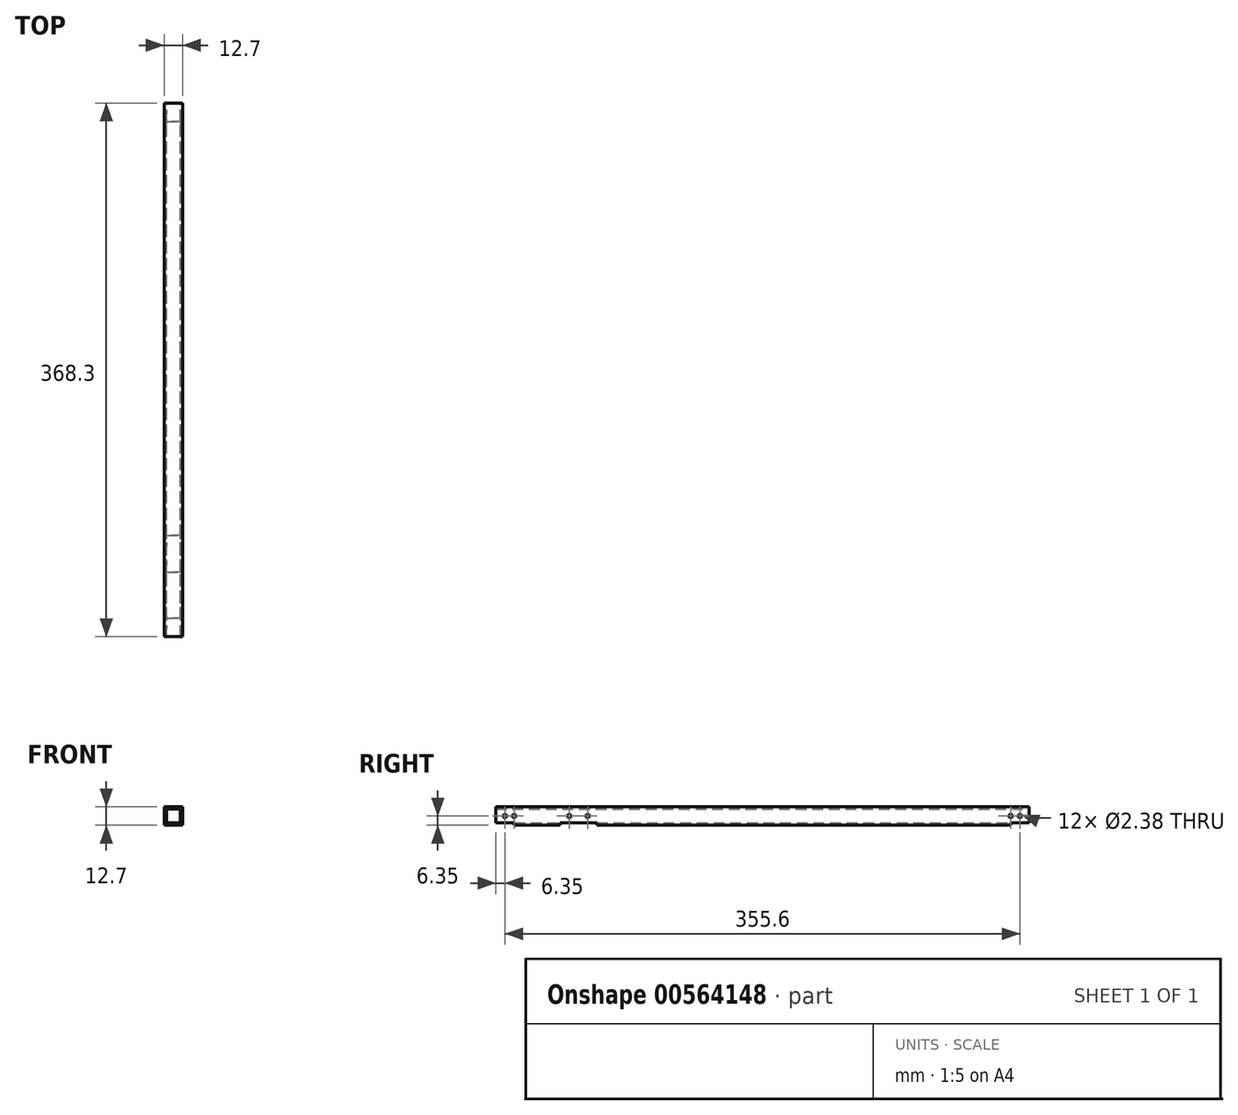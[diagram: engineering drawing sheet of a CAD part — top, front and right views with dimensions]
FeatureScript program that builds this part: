
annotation { "Feature Type Name" : "Feature", "Feature Type Description" : "" }
export const myFeature = defineFeature(function(context is Context, id is Id, definition is map)
    precondition{}
    {
        {
            var Q0;
            Q0=qCreatedBy(makeId("Front.planeOp"),FACE);
            var sketch = newSketch(context, id + "F0", { "sketchPlane" : qUnion([Q0])});
            skLineSegment(sketch, "E0.bottom", {"start": v(4.76, 4.76) * mm, "end": v(-4.76, 4.76) * mm});
            skLineSegment(sketch, "E0.top", {"start": v(4.76, -4.76) * mm, "end": v(-4.76, -4.76) * mm});
            skLineSegment(sketch, "E0.left", {"start": v(4.76, 4.76) * mm, "end": v(4.76, -4.76) * mm});
            skLineSegment(sketch, "E0.right", {"start": v(-4.76, 4.76) * mm, "end": v(-4.76, -4.76) * mm});
            skPoint(sketch, "E0.middle", {"position": v(0, 0) * mm});
            skLineSegment(sketch, "E1.bottom", {"start": v(6.35, 6.35) * mm, "end": v(-6.35, 6.35) * mm});
            skLineSegment(sketch, "E1.top", {"start": v(6.35, -6.35) * mm, "end": v(-6.35, -6.35) * mm});
            skLineSegment(sketch, "E1.left", {"start": v(6.35, 6.35) * mm, "end": v(6.35, -6.35) * mm});
            skLineSegment(sketch, "E1.right", {"start": v(-6.35, 6.35) * mm, "end": v(-6.35, -6.35) * mm});
            skLineSegment(sketch, "E2", {"start": v(0, 4.76) * mm, "end": v(0, 6.35) * mm});
            skLineSegment(sketch, "E3", {"start": v(4.76, 0) * mm, "end": v(6.35, 0) * mm});
            skSolve(sketch);
        }
        {
            var Q0;
            Q0 = qSketchRegion(id + "F0", true);
            extrude(context, id + "F1", {"entities" : qUnion([Q0]), "depth" : 368.3 * mm, "offsetDistance" : 25.4 * mm});
        }
        {
            var Q0;
            Q0=makeQuery(id+"F1.opExtrude","SWEPT_FACE",FACE,{"disambiguationData":[OSD([sQuery(id+"F0.wireOp",EDGE,"E1.left")])]});
            var sketch = newSketch(context, id + "F2", { "sketchPlane" : qUnion([Q0])});
            skPoint(sketch, "E4.centerSnap0", {"position": v(-368.3, 0) * mm});
            skLineSegment(sketch, "E5", {"start": v(-311.15, 6.35) * mm, "end": v(-311.15, -6.35) * mm});
            skCircle(sketch, "E6", {"center": v(-317.5, 0) * mm, "radius": 1.2 * mm});
            skCircle(sketch, "E7.MirrorC", {"center": v(-304.8, 0) * mm, "radius": 1.2 * mm});
            skCircle(sketch, "E8", {"center": v(-361.95, 0) * mm, "radius": 1.2 * mm});
            skCircle(sketch, "E9", {"center": v(-355.6, 0) * mm, "radius": 1.2 * mm});
            skLineSegment(sketch, "E10", {"start": v(-184.15, 6.35) * mm, "end": v(-184.15, -6.35) * mm});
            skCircle(sketch, "E11.MirrorC", {"center": v(-6.35, 0) * mm, "radius": 1.2 * mm});
            skCircle(sketch, "E12.MirrorC", {"center": v(-12.7, 0) * mm, "radius": 1.2 * mm});
            skSolve(sketch);
        }
        {
            var Q0;
            Q0 = qSketchRegion(id + "F2", true);
            extrude(context, id + "F3", {"entities" : qUnion([Q0]), "operationType" : NewBodyOperationType.REMOVE, "endBound" : BoundingType.THROUGH_ALL, "oppositeDirection" : true, "depth" : 25.4 * mm, "offsetDistance" : 25.4 * mm});
        }
        {
            var Q0;
            Q0=makeQuery(id+"F1.opExtrude","SWEPT_FACE",FACE,{"disambiguationData":[OSD([sQuery(id+"F0.wireOp",EDGE,"E1.top")])]});
            var sketch = newSketch(context, id + "F4", { "sketchPlane" : qUnion([Q0])});
            skLineSegment(sketch, "E13.bottom", {"start": v(6.35, 323.85) * mm, "end": v(-6.35, 323.85) * mm});
            skLineSegment(sketch, "E13.top", {"start": v(6.35, 298.45) * mm, "end": v(-6.35, 298.45) * mm});
            skLineSegment(sketch, "E13.left", {"start": v(6.35, 323.85) * mm, "end": v(6.35, 298.45) * mm});
            skLineSegment(sketch, "E13.right", {"start": v(-6.35, 323.85) * mm, "end": v(-6.35, 298.45) * mm});
            skPoint(sketch, "E13.middle", {"position": v(0, 311.15) * mm});
            skLineSegment(sketch, "E14.bottom", {"start": v(6.35, 368.3) * mm, "end": v(-6.35, 368.3) * mm});
            skLineSegment(sketch, "E14.top", {"start": v(6.35, 355.6) * mm, "end": v(-6.35, 355.6) * mm});
            skLineSegment(sketch, "E14.left", {"start": v(6.35, 368.3) * mm, "end": v(6.35, 355.6) * mm});
            skLineSegment(sketch, "E14.right", {"start": v(-6.35, 368.3) * mm, "end": v(-6.35, 355.6) * mm});
            skLineSegment(sketch, "E15", {"start": v(6.35, 184.15) * mm, "end": v(-6.35, 184.15) * mm});
            skLineSegment(sketch, "E16.MirrorCS", {"start": v(6.35, 0) * mm, "end": v(-6.35, 0) * mm});
            skLineSegment(sketch, "E17.MirrorCS", {"start": v(6.35, 0) * mm, "end": v(6.35, 12.7) * mm});
            skLineSegment(sketch, "E18.MirrorCS", {"start": v(-6.35, 0) * mm, "end": v(-6.35, 12.7) * mm});
            skLineSegment(sketch, "E19.MirrorCS", {"start": v(6.35, 12.7) * mm, "end": v(-6.35, 12.7) * mm});
            skSolve(sketch);
        }
        {
            var Q0;
            Q0 = qSketchRegion(id + "F4", true);
            var Q1;
            Q1=makeQuery(id+"F1.opExtrude","SWEPT_FACE",FACE,{"disambiguationData":[OSD([sQuery(id+"F0.wireOp",EDGE,"E0.top")])]});
            extrude(context, id + "F5", {"entities" : qUnion([Q0]), "operationType" : NewBodyOperationType.REMOVE, "endBound" : BoundingType.UP_TO_SURFACE, "oppositeDirection" : true, "depth" : 25.4 * mm, "endBoundEntityFace" : qUnion([Q1]), "offsetDistance" : 25.4 * mm});
        }
    });
